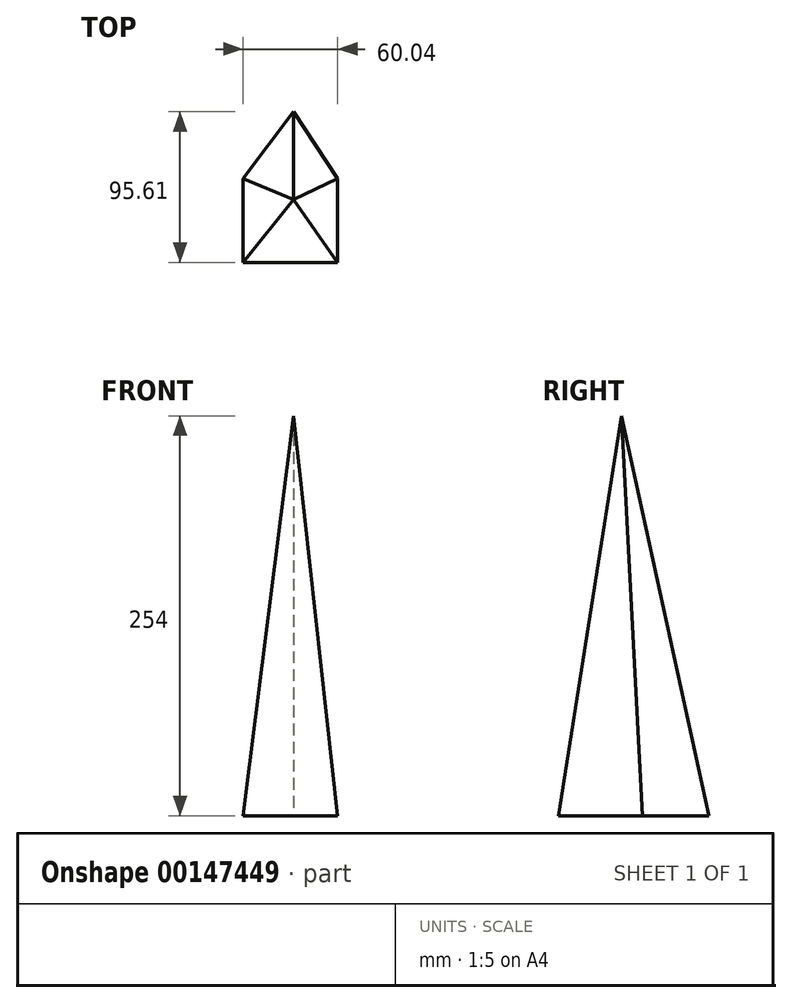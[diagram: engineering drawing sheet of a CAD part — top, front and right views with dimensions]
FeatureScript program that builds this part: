
annotation { "Feature Type Name" : "Feature", "Feature Type Description" : "" }
export const myFeature = defineFeature(function(context is Context, id is Id, definition is map)
    precondition{}
    {
        {
            var Q0;
            Q0=qCreatedBy(makeId("Top.planeOp"),FACE);
            var sketch = newSketch(context, id + "F0", { "sketchPlane" : qUnion([Q0])});
            skLineSegment(sketch, "E0", {"start": v(0, 55.82) * mm, "end": v(-32.06, 13.55) * mm});
            skLineSegment(sketch, "E1", {"start": v(-32.06, 13.55) * mm, "end": v(-32.06, -39.79) * mm});
            skLineSegment(sketch, "E2", {"start": v(-32.06, -39.79) * mm, "end": v(27.98, -39.79) * mm});
            skLineSegment(sketch, "E3", {"start": v(27.98, -39.79) * mm, "end": v(27.98, 13.55) * mm});
            skLineSegment(sketch, "E4", {"start": v(27.98, 13.55) * mm, "end": v(0, 55.82) * mm});
            skSolve(sketch);
        }
        {
            var Q0;
            Q0=qCreatedBy(makeId("Top.planeOp"),FACE);
            cPlane(context, id + "F1", {"entities" : qUnion([Q0]), "cplaneType" : CPlaneType.OFFSET, "offset" : 254 * mm, "width" : 152.4 * mm, "height" : 152.4 * mm});
        }
        {
            var Q0;
            Q0=qCreatedBy(id+"F1.planeOp",FACE);
            var sketch = newSketch(context, id + "F2", { "sketchPlane" : qUnion([Q0])});
            skPoint(sketch, "E5", {"position": v(0, 0) * mm});
            skSolve(sketch);
        }
        {
            var Q0;
            Q0=sQuery(id+"F2.wireOp",VERTEX,"E5");
            var Q1;
            Q1=makeQuery(id+"F0.imprint","IMPRINT",FACE,{"disambiguationData":[TD([[makeQuery(id+"F0.imprint","IMPRINT",EDGE,{"derivedFrom":sQuery(id+"F0.wireOp",EDGE,"E0")}),1.0]])]});
            loft(context, id + "F3", {"sheetProfilesArray" : [{ "sheetProfileEntities" : qUnion([Q0]) }, { "sheetProfileEntities" : qUnion([Q1]) }]});
        }
    });
